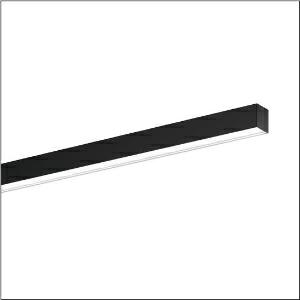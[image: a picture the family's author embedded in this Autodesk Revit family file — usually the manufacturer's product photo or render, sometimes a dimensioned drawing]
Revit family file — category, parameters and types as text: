
# Revit family: silica_r__21_51mx20db32bb_e5b9
name_source: partatom
category: Lighting Fixtures
units: mm (PartAtom-declared; Revit-internal decimal feet)

## family parameters
Cut with Voids When Loaded = No
Host = Face
Light Source = No
Part Type = Normal
Room Calculation Point = No
Round Connector Dimension = Use Diameter
Shared = No

## types (1)
- --- (1 x LED, 3000 lm, 20.2 W, 3000K)
    Apparent Load = 20 VA
    CIE Flux Codes = 48 79 96 100 100
    Color Rendering = 80
    Color Temperature = 3000K
    Default Elevation = 1800 mm
    Description = Silica® 21, office luminaire, primary optical cover: cover, of PMMA, opal, light emission: direct distribution, primary light characteristic: symmetric, installation type: surface-mounted, LED, rated luminous flux: 3.000lm, luminous efficacy: 149lm/W, light colour: 830, colour temperature: 3000K, with terminal, 3+2-pole, max. 2.5mm², mains connection: 220..240V, AC, 50/60Hz, luminaire housing, of aluminium, jet black (RAL 9005), length: 1.504mm, width: 53mm, height: 53mm, protection rating (complete): IP20, insulation class (complete): insulation class I (protective earthing), certification: CE, permissible operating ambient temperature: 0..+35°C, standard: EN 50419, packaging unit: 1 piece
    Height = 0 mm  [stored 0 ft]
    Lamp = 1 x LED
    Lamp Light Flux = 3000 lm
    Lamp Power = 20.2 W
    Lamp count = 1
    Length = 1504 mm
    Luminous efficacy = 149 lm/W
    Manufacturer = Siteco
    ModVariant = No
    Model = 51MX20DB32BB
    Mounting Place = Ceiling
    Mounting Type = Recessed
    Number of Poles = 1
    OnlyDefault = Yes
    Power Factor = 1
    Product Name = Silica® 21
    Product group = office luminaire | ceiling recessed
    ProductGroupID = 401
    Protection Class = Protection class I
    Protection Degree = IP 20
    RLX_Detail_Level = 1
    RLX_Emergency_Light_Flux = 0 lm
    RLX_Emergency_Type = 0
    RLX_Emergency_Type_DB = No
    RlxData = <blob elided: 28445 chars, md5=3eadde25>
    Socket = socket
    Standby Power = 0 W
    System Light Flux = 3000 lm
    System Power = 20 W
    Type Comments = factory setting: luminous flux: 100 % | dim-lin: 254 | 233 mA
    Type Image = l_1297760.jpg
    URL = http://relux.com
    VarID = @adj_048249
    Voltage = 0 V
    Weight = 0.00 kg
    Width = 53 mm

note: [stored X ft] marks values corroborated as IEEE doubles in the binary element streams (Revit-internal decimal feet)

## geometry (parser evidence)
native form markers: Blend x4, Sweep x10
no freeform markers — native parametric forms only
